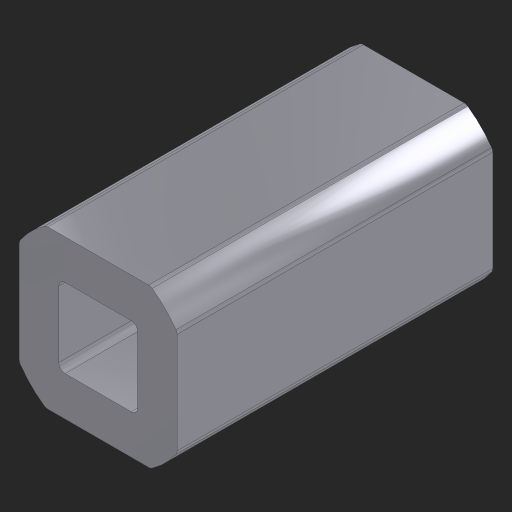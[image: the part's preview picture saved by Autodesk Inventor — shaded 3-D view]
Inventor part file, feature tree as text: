
AUTODESK INVENTOR PART (.ipt)
format: ipt  version: 2023 (Build 270158000, 158)  size: 154,112 bytes
history: native  units: in
note: dims shown in document units (in); Inventor stores cm internally (conversion verified against a paired STEP export)
features: extrude x2, sketch x2, fillet x1
ambient origin geometry x8: Origin, YZ Plane, XZ Plane, XY Plane, X Axis, Y Axis, Z Axis, Center Point
bodies: Solid1 (feature_tree)
feature tree (5):
  extrude  "Extrusion1"  Depth=0.25in
  extrude  "Extrusion2"  Depth=0.5in TaperAngle=0.0deg
  fillet  "Fillet1"  Radius=0.125in
  sketch  "Sketch1"  dims[d0=0.3in d1=0.25in]
  sketch  "Sketch2"  dims[d2=0.5in d3=0.0in d5=0.5in d6=0.0in d7=0.125in d8=0.01in]
